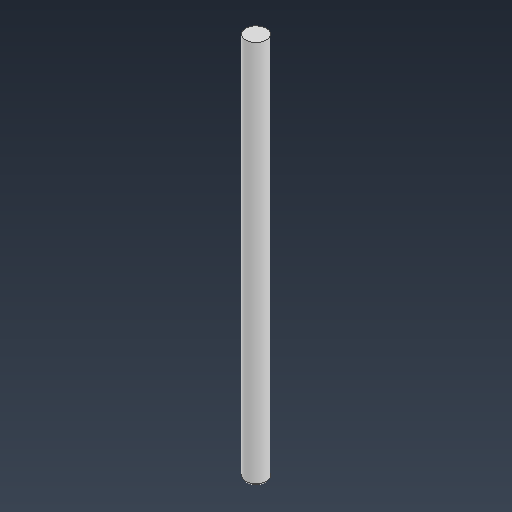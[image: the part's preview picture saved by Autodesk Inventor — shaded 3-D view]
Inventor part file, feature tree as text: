
AUTODESK INVENTOR PART (.ipt)
format: ipt  version: 2021 (Build 250183000, 183)  size: 92,672 bytes
history: native  units: mm
features: other x2, extrude x1, fillet x1, sketch x1
ambient origin geometry x8: Origin, YZ Plane, XZ Plane, XY Plane, X Axis, Y Axis, Z Axis, Center Point
bodies: Body1 (feature_tree)
feature tree (5):
  other  "Rotor"
  other  "Sólido1"
  extrude  "Extrusão1"  Depth=18.6mm TaperAngle=0.0deg
  fillet  "Arredondamento2"  Radius=0.1mm
  sketch  "Esboço1"  dims[d0=1.0mm d1=18.6mm d2=0.0mm d4=0.1mm]
